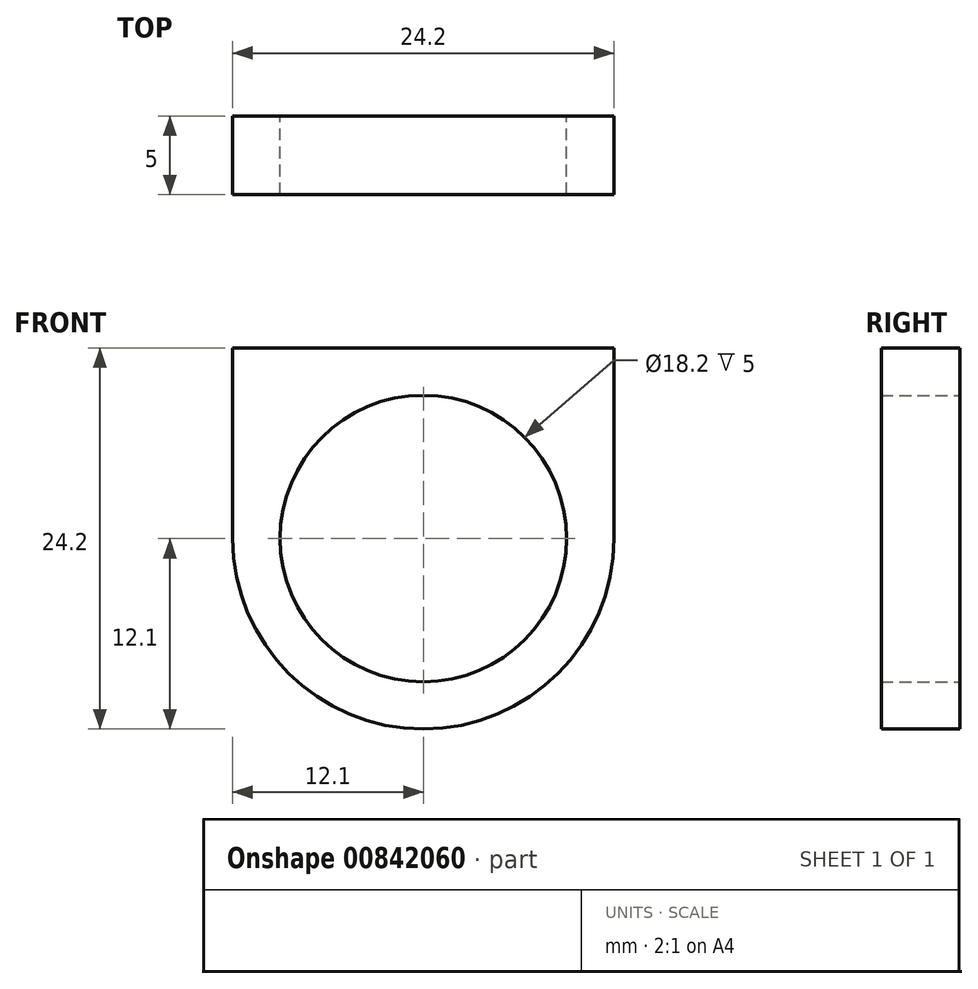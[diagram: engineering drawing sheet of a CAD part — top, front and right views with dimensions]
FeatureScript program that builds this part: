
annotation { "Feature Type Name" : "Feature", "Feature Type Description" : "" }
export const myFeature = defineFeature(function(context is Context, id is Id, definition is map)
    precondition{}
    {
        {
            var Q0;
            Q0=qCreatedBy(makeId("Front.planeOp"),FACE);
            var sketch = newSketch(context, id + "F0", { "sketchPlane" : qUnion([Q0])});
            skCircle(sketch, "E0", {"center": v(0, 0) * mm, "radius": 9.1 * mm});
            skCircle(sketch, "E1", {"center": v(0, 0) * mm, "radius": 12.1 * mm});
            skLineSegment(sketch, "E2", {"start": v(-12.1, 0) * mm, "end": v(-12.1, 12.1) * mm});
            skLineSegment(sketch, "E3", {"start": v(12.1, 0) * mm, "end": v(12.1, 12.1) * mm});
            skLineSegment(sketch, "E4", {"start": v(-12.1, 12.1) * mm, "end": v(12.1, 12.1) * mm});
            skSolve(sketch);
        }
        {
            var Q0;
            Q0 = qSketchRegion(id + "F0", true);
            extrude(context, id + "F1", {"entities" : qUnion([Q0]), "depth" : 2.5 * mm, "offsetDistance" : 25 * mm});
        }
        {
            var Q0;
            Q0=makeQuery(id+"F1.opExtrude","SWEPT_BODY",BODY,{"disambiguationData":[OSD([sQuery(id+"F0.wireOp",EDGE,"E0"),sQuery(id+"F0.wireOp",EDGE,"E1")])]});
            var Q1;
            Q1=qCreatedBy(makeId("Front.planeOp"),FACE);
            mirror(context, id + "F2", {"operationType" : NewBodyOperationType.ADD, "entities" : qUnion([Q0]), "mirrorPlane" : qUnion([Q1])});
        }
    });
